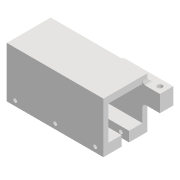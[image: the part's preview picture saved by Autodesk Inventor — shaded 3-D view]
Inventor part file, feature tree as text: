
AUTODESK INVENTOR PART (.ipt)
format: ipt  version: 2022 (Build 260153000, 153)  size: 232,960 bytes
history: native  units: mm
features: extrude x7, sketch x7, projected_geometry x5, fillet x2
ambient origin geometry x8: Origin, YZ Plane, XZ Plane, XY Plane, X Axis, Y Axis, Z Axis, Center Point
bodies: Solid1 (feature_tree)
feature tree (21):
  extrude  "Extrusion1"  Depth=20.4mm
  extrude  "Extrusion3"  Depth=54.8mm TaperAngle=0.0deg
  extrude  "Extrusion8"  Depth=3.0mm
  extrude  "Extrusion9"  Depth=8.0mm
  fillet  "Fillet3"  Radius=8.0mm
  extrude  "Extrusion10"  Depth=10.0mm
  extrude  "Extrusion11"  TaperAngle=0.0deg  [1 undecoded]
  extrude  "Extrusion12"  Depth=3.0mm TaperAngle=0.0deg
  fillet  "Fillet4"  Radius=3.0mm
  sketch  "Sketch2"  dims[d5=20.4mm d6=20.4mm]
  sketch  "Sketch4"  dims[d8=6.0mm d9=54.8mm d10=0.0mm]
  projected_geometry  "Projected Loop2"
  sketch  "Sketch10"  dims[d22=4.0mm d23=3.0mm]
  projected_geometry  "Projected Loop8"
  sketch  "Sketch11"  dims[d24=3.0mm d27=8.0mm d28=8.0mm]
  projected_geometry  "Projected Loop9"
  projected_geometry  "Projected Loop10"
  sketch  "Sketch12"  dims[d29=10.0mm d30=11.25mm]
  projected_geometry  "Projected Loop11"
  sketch  "Sketch13"  dims[d31=40.0mm d32=0.0mm]
  sketch  "Sketch14"  dims[d33=5.0mm d34=0.0mm d49=3.0mm d50=0.0mm d55=3.0mm d56=4.0mm d57=4.0mm d58=10.0mm d59=0.0mm d61=15.0mm d62=0.0mm d63=2.0mm d64=2.2mm d65=5.0mm d66=3.0mm d67=2.2mm d68=2.2mm d69=5.0mm d70=3.0mm d71=29.0mm d72=3.0mm d73=100.0mm d74=0.0mm d75=4.0mm d76=4.0mm d77=46.8mm d78=27.0mm d79=0.0mm d80=2.6mm d81=11.0mm d82=2.6mm d83=23.0mm d84=6.25mm d85=6.25mm d86=2.6mm d87=2.6mm d88=11.0mm d89=23.0mm d90=6.25mm d91=6.25mm d92=100.0mm d93=0.0mm d94=2.0mm]
note: 1 required parameter value undecoded (feature->parameter linkage not recoverable at this tier; creation-order binding heuristic only, values carry confidence <= 0.55)
